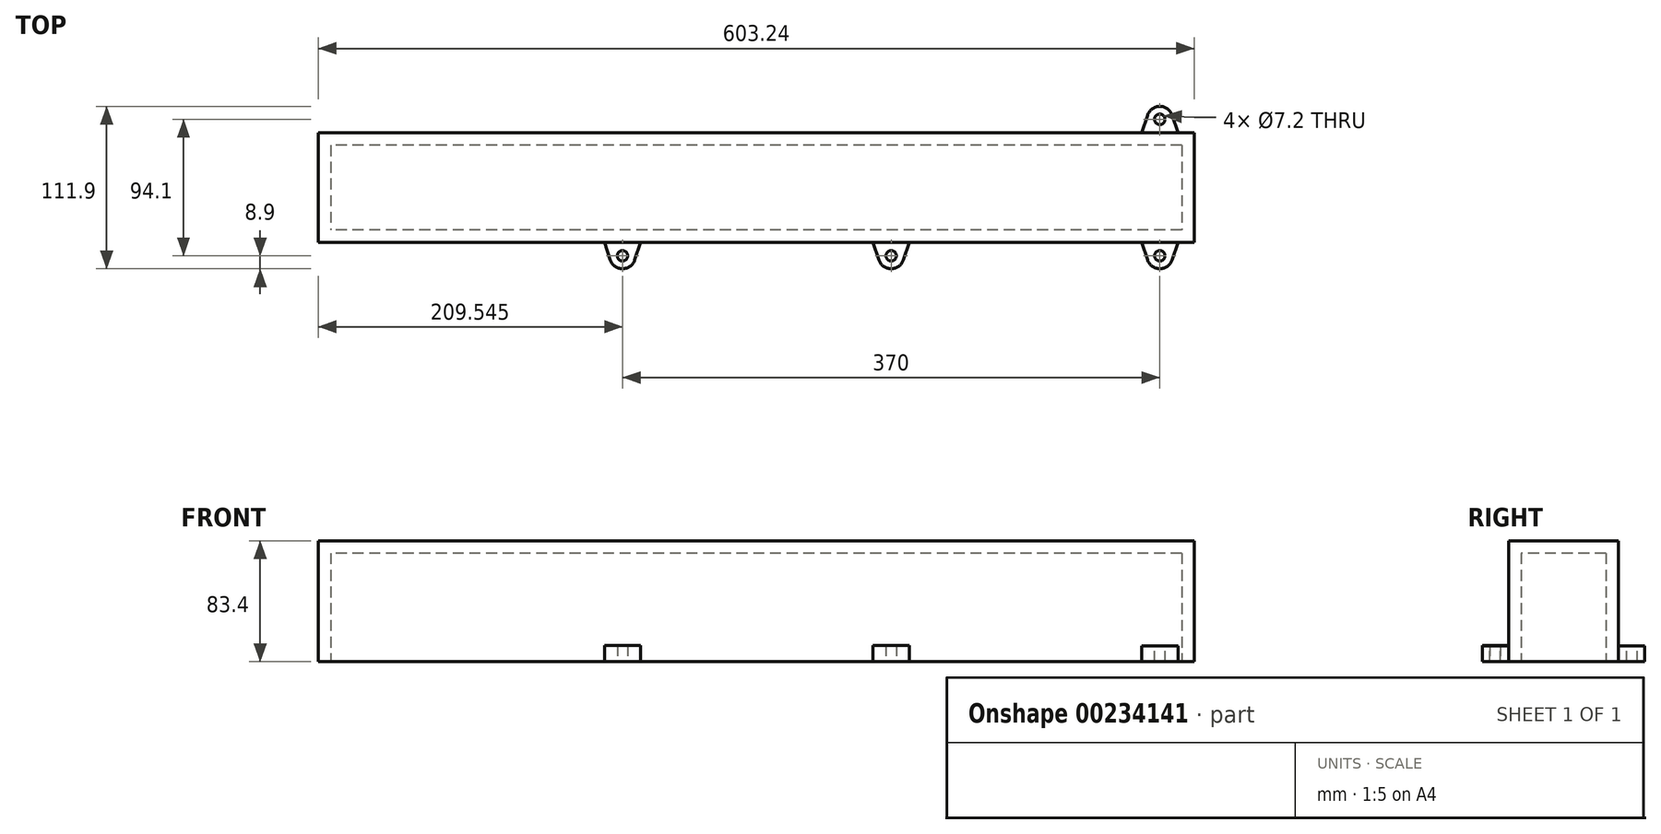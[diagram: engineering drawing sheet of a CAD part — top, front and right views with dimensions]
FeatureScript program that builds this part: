
annotation { "Feature Type Name" : "Feature", "Feature Type Description" : "" }
export const myFeature = defineFeature(function(context is Context, id is Id, definition is map)
    precondition{}
    {
        {
            var Q0;
            Q0=qCreatedBy(makeId("Top.planeOp"),FACE);
            var sketch = newSketch(context, id + "F0", { "sketchPlane" : qUnion([Q0])});
            skLineSegment(sketch, "E0.bottom", {"start": v(301.63, 37.8) * mm, "end": v(-301.63, 37.8) * mm});
            skLineSegment(sketch, "E0.top", {"start": v(301.63, -37.8) * mm, "end": v(-301.63, -37.8) * mm});
            skLineSegment(sketch, "E0.left", {"start": v(301.63, 37.8) * mm, "end": v(301.63, -37.8) * mm});
            skLineSegment(sketch, "E0.right", {"start": v(-301.63, 37.8) * mm, "end": v(-301.63, -37.8) * mm});
            skPoint(sketch, "E0.middle", {"position": v(0, 0) * mm});
            skSolve(sketch);
        }
        {
            var Q0;
            Q0 = qSketchRegion(id + "F0", true);
            extrude(context, id + "F1", {"entities" : qUnion([Q0]), "depth" : 83.4 * mm});
        }
        {
            var Q0;
            Q0=makeQuery(id+"F1.opExtrude","CAP_FACE",FACE,{"disambiguationData":[OSD([sQuery(id+"F0.wireOp",EDGE,"E0.bottom"),sQuery(id+"F0.wireOp",EDGE,"E0.top"),sQuery(id+"F0.wireOp",EDGE,"E0.left"),sQuery(id+"F0.wireOp",EDGE,"E0.right")])],"isStart":true});
            shell(context, id + "F2", {"entities" : qUnion([Q0]), "thickness" : 8.6 * mm});
        }
        {
            var Q0;
            Q0=makeQuery(id+"F1.opExtrude","CAP_FACE",FACE,{"disambiguationData":[OSD([sQuery(id+"F0.wireOp",EDGE,"E0.bottom"),sQuery(id+"F0.wireOp",EDGE,"E0.top"),sQuery(id+"F0.wireOp",EDGE,"E0.left"),sQuery(id+"F0.wireOp",EDGE,"E0.right")])],"isStart":false});
            var sketch = newSketch(context, id + "F3", { "sketchPlane" : qUnion([Q0])});
            skLineSegment(sketch, "E1", {"start": v(301.63, 30.01) * mm, "end": v(277.93, 30.01) * mm});
            skLineSegment(sketch, "E2", {"start": v(277.93, 56.58) * mm, "end": v(277.93, -64.5) * mm, "construction": true});
            skCircle(sketch, "E3", {"center": v(277.93, 47.05) * mm, "radius": 3.6 * mm});
            skLineSegment(sketch, "E4", {"start": v(301.63, 33.55) * mm, "end": v(237.17, 33.55) * mm, "construction": true});
            skArc(sketch, "E5.0", {"start": v(286.36, 49.89) * mm, "mid": v(277.93, 55.95) * mm, "end": v(269.49, 49.89) * mm});
            skLineSegment(sketch, "E6", {"start": v(290.43, 37.8) * mm, "end": v(286.36, 49.89) * mm});
            skLineSegment(sketch, "E7.MirrorCS", {"start": v(265.43, 37.8) * mm, "end": v(269.49, 49.89) * mm});
            skLineSegment(sketch, "E8", {"start": v(265.43, 37.8) * mm, "end": v(290.43, 37.8) * mm});
            skLineSegment(sketch, "E9", {"start": v(301.63, 0) * mm, "end": v(-301.63, 0) * mm, "construction": true});
            skLineSegment(sketch, "E10.MirrorCS", {"start": v(265.43, -37.8) * mm, "end": v(290.43, -37.8) * mm});
            skLineSegment(sketch, "E11.MirrorCS", {"start": v(265.43, -37.8) * mm, "end": v(269.49, -49.89) * mm});
            skArc(sketch, "E12.MirrorCS", {"start": v(286.36, -49.89) * mm, "mid": v(277.93, -55.95) * mm, "end": v(269.49, -49.89) * mm});
            skLineSegment(sketch, "E13.MirrorCS", {"start": v(290.43, -37.8) * mm, "end": v(286.36, -49.89) * mm});
            skCircle(sketch, "E14.MirrorC", {"center": v(277.93, -47.05) * mm, "radius": 3.6 * mm});
            skSolve(sketch);
        }
        {
            var Q0;
            Q0 = qSketchRegion(id + "F3", true);
            var Q1;
            Q1=makeQuery(id+"F1.opExtrude","SWEPT_BODY",BODY,{"disambiguationData":[OSD([sQuery(id+"F0.wireOp",EDGE,"E0.bottom"),sQuery(id+"F0.wireOp",EDGE,"E0.top"),sQuery(id+"F0.wireOp",EDGE,"E0.left"),sQuery(id+"F0.wireOp",EDGE,"E0.right")])]});
            extrude(context, id + "F4", {"entities" : qUnion([Q0]), "operationType" : NewBodyOperationType.ADD, "oppositeDirection" : true, "depth" : 83.4 * mm, "hasSecondDirection" : true, "secondDirectionOppositeDirection" : true, "secondDirectionBoundEntityBody" : qUnion([Q1]), "secondDirectionDepth" : 72.4 * mm});
        }
        {
            var Q0;
            Q0=makeQuery(id+"F4.boolean.opBoolean","MERGE",FACE,{"derivedFrom":[makeQuery(id+"F1.opExtrude","CAP_FACE",FACE,{"disambiguationData":[OSD([sQuery(id+"F0.wireOp",EDGE,"E0.bottom"),sQuery(id+"F0.wireOp",EDGE,"E0.top"),sQuery(id+"F0.wireOp",EDGE,"E0.left"),sQuery(id+"F0.wireOp",EDGE,"E0.right")])],"isStart":true}),makeQuery(id+"F4.opExtrude","CAP_FACE",FACE,{"disambiguationData":[OSD([sQuery(id+"F3.wireOp",EDGE,"E3"),sQuery(id+"F3.wireOp",EDGE,"E5.0"),sQuery(id+"F3.wireOp",EDGE,"E6"),sQuery(id+"F3.wireOp",EDGE,"E7.MirrorCS"),sQuery(id+"F3.wireOp",EDGE,"E8")])],"isStart":false}),makeQuery(id+"F4.opExtrude","CAP_FACE",FACE,{"disambiguationData":[OSD([sQuery(id+"F3.wireOp",EDGE,"E10.MirrorCS"),sQuery(id+"F3.wireOp",EDGE,"E11.MirrorCS"),sQuery(id+"F3.wireOp",EDGE,"E12.MirrorCS"),sQuery(id+"F3.wireOp",EDGE,"E13.MirrorCS"),sQuery(id+"F3.wireOp",EDGE,"E14.MirrorC")])],"isStart":false})]});
            var sketch = newSketch(context, id + "F5", { "sketchPlane" : qUnion([Q0])});
            skLineSegment(sketch, "E15", {"start": v(277.93, 47.05) * mm, "end": v(92.93, 47.05) * mm, "construction": true});
            skLineSegment(sketch, "E16", {"start": v(277.93, 47.05) * mm, "end": v(185.43, 47.05) * mm, "construction": true});
            skLineSegment(sketch, "E17", {"start": v(185.43, 100.56) * mm, "end": v(185.43, -71.43) * mm, "construction": true});
            skLineSegment(sketch, "E18.0", {"start": v(268.54, 47.05) * mm, "end": v(269.49, 49.89) * mm});
            skLineSegment(sketch, "E19.MirrorCS", {"start": v(105.42, 37.8) * mm, "end": v(101.36, 49.89) * mm});
            skArc(sketch, "E20.MirrorCS", {"start": v(84.49, 49.89) * mm, "mid": v(92.93, 55.95) * mm, "end": v(101.36, 49.89) * mm});
            skLineSegment(sketch, "E21.MirrorCS", {"start": v(80.42, 37.8) * mm, "end": v(84.49, 49.89) * mm});
            skCircle(sketch, "E22.MirrorC", {"center": v(92.93, 47.05) * mm, "radius": 3.6 * mm});
            skLineSegment(sketch, "E23", {"start": v(80.42, 37.8) * mm, "end": v(105.42, 37.8) * mm});
            skLineSegment(sketch, "E24", {"start": v(92.93, 47.05) * mm, "end": v(-92.07, 47.05) * mm, "construction": true});
            skLineSegment(sketch, "E25", {"start": v(92.93, 47.05) * mm, "end": v(0.43, 47.05) * mm, "construction": true});
            skLineSegment(sketch, "E26", {"start": v(0.43, 85.95) * mm, "end": v(0, -55.7) * mm, "construction": true});
            skLineSegment(sketch, "E27", {"start": v(92.93, 87.44) * mm, "end": v(92.93, -20.77) * mm, "construction": true});
            skLineSegment(sketch, "E28.MirrorCS", {"start": v(-79.58, 37.8) * mm, "end": v(-83.64, 49.89) * mm});
            skArc(sketch, "E29.MirrorCS", {"start": v(-100.51, 49.89) * mm, "mid": v(-92.07, 55.95) * mm, "end": v(-83.64, 49.89) * mm});
            skLineSegment(sketch, "E30.MirrorCS", {"start": v(-104.58, 37.8) * mm, "end": v(-100.51, 49.89) * mm});
            skCircle(sketch, "E31.MirrorC", {"center": v(-92.07, 47.05) * mm, "radius": 3.6 * mm});
            skLineSegment(sketch, "E32", {"start": v(-104.58, 37.8) * mm, "end": v(-79.58, 37.8) * mm, "construction": true});
            skPoint(sketch, "E33.orphan", {"position": v(265.43, 37.8) * mm});
            skPoint(sketch, "E34.0.end.orphan", {"position": v(269.49, 49.89) * mm});
            skPoint(sketch, "E34.0.start.orphan", {"position": v(286.36, 49.89) * mm});
            skPoint(sketch, "E35.0.start.orphan", {"position": v(290.43, 37.8) * mm});
            skLineSegment(sketch, "E36", {"start": v(-104.58, 37.8) * mm, "end": v(-79.58, 37.8) * mm});
            skSolve(sketch);
        }
        {
            var Q0;
            Q0 = qSketchRegion(id + "F5", true);
            extrude(context, id + "F6", {"entities" : qUnion([Q0]), "operationType" : NewBodyOperationType.ADD, "oppositeDirection" : true, "depth" : 11.3 * mm});
        }
    });
